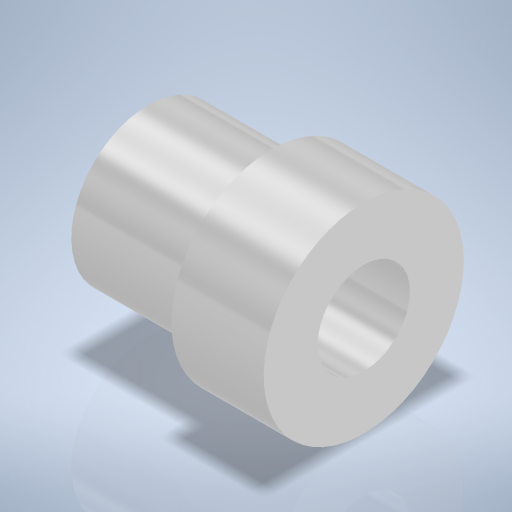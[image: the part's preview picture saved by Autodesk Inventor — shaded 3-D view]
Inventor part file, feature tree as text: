
AUTODESK INVENTOR PART (.ipt)
format: ipt  version: 2024 (Build 280153000, 153)  size: 257,024 bytes
history: native  units: mm
features: sketch x2, revolve x1, hole x1
ambient origin geometry x8: Origin, YZ Plane, XZ Plane, XY Plane, X Axis, Y Axis, Z Axis, Center Point
bodies: Volumenkörper1 (feature_tree)
feature tree (4):
  revolve  "Umdrehung1"
  hole  "Bohrung1"  [1 undecoded]
  sketch  "Skizze1"  dims[d0=6.0mm d1=8.0mm]
  sketch  "Skizze2"  dims[d2=10.0mm d3=13.0mm d4=90.0deg d5=6.0mm d6=6.0mm d7=4.0mm d8=2.0mm d9=90.0deg d10=26.0mm d11=0.0mm]
note: 1 required parameter value undecoded (feature->parameter linkage not recoverable at this tier; creation-order binding heuristic only, values carry confidence <= 0.55)
